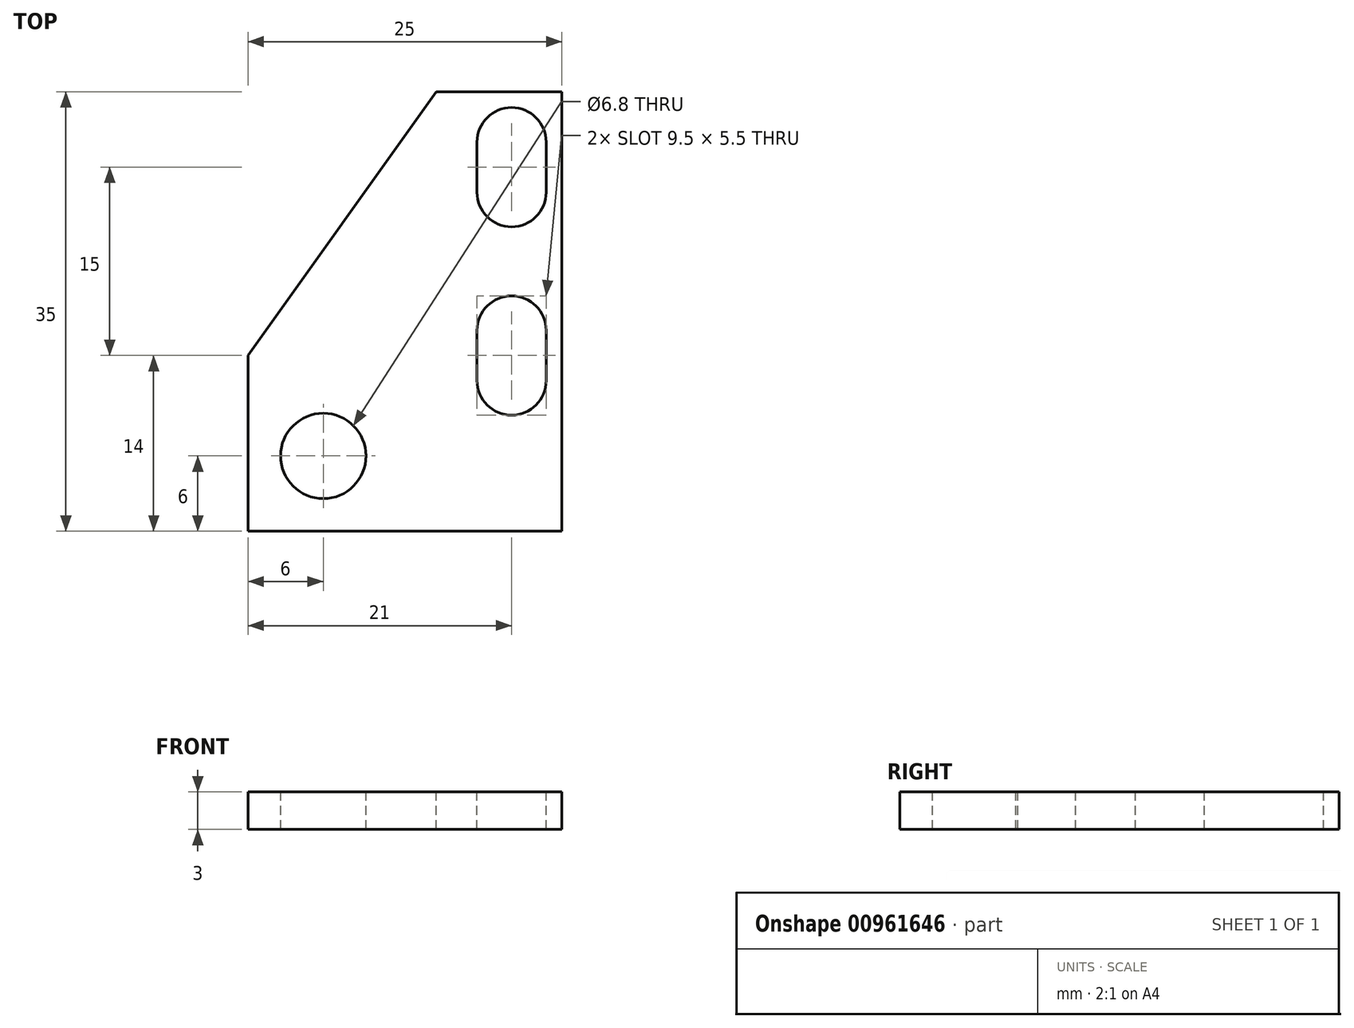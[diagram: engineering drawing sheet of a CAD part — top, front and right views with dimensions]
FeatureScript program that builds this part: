
annotation { "Feature Type Name" : "Feature", "Feature Type Description" : "" }
export const myFeature = defineFeature(function(context is Context, id is Id, definition is map)
    precondition{}
    {
        {
            var Q0;
            Q0=qCreatedBy(makeId("Top.planeOp"),FACE);
            var sketch = newSketch(context, id + "F0", { "sketchPlane" : qUnion([Q0])});
            skLineSegment(sketch, "E0.bottom", {"start": v(0, 0) * mm, "end": v(25, 0) * mm});
            skLineSegment(sketch, "E0.top", {"start": v(0, -35) * mm, "end": v(25, -35) * mm});
            skLineSegment(sketch, "E0.left", {"start": v(0, 0) * mm, "end": v(0, -35) * mm});
            skLineSegment(sketch, "E0.right", {"start": v(25, 0) * mm, "end": v(25, -35) * mm});
            skSolve(sketch);
        }
        {
            var Q0;
            Q0=makeQuery(id+"F0.imprint","IMPRINT",FACE,{"disambiguationData":[TD([[makeQuery(id+"F0.imprint","IMPRINT",EDGE,{"derivedFrom":sQuery(id+"F0.wireOp",EDGE,"E0.bottom")}),-1.0]])]});
            extrude(context, id + "F1", {"entities" : qUnion([Q0]), "depth" : 3 * mm, "offsetDistance" : 25 * mm});
        }
        {
            var Q0;
            Q0=makeQuery(id+"F1.opExtrude","CAP_FACE",FACE,{"disambiguationData":[OSD([sQuery(id+"F0.wireOp",EDGE,"E0.bottom"),sQuery(id+"F0.wireOp",EDGE,"E0.top"),sQuery(id+"F0.wireOp",EDGE,"E0.left"),sQuery(id+"F0.wireOp",EDGE,"E0.right")])],"isStart":false});
            var sketch = newSketch(context, id + "F2", { "sketchPlane" : qUnion([Q0])});
            skPoint(sketch, "E1", {"position": v(21, -4) * mm});
            skPoint(sketch, "E2", {"position": v(21, -19) * mm});
            skPoint(sketch, "E3", {"position": v(0, -35) * mm});
            skPoint(sketch, "E4", {"position": v(6, -29) * mm});
            skPoint(sketch, "E5", {"position": v(21, -8) * mm});
            skPoint(sketch, "E6", {"position": v(21, -23) * mm});
            skPoint(sketch, "E7", {"position": v(17.74, 0) * mm});
            skCircle(sketch, "E8", {"center": v(21, -4) * mm, "radius": 2.75 * mm});
            skCircle(sketch, "E9", {"center": v(21, -8) * mm, "radius": 2.75 * mm});
            skCircle(sketch, "E10", {"center": v(21, -19) * mm, "radius": 2.75 * mm});
            skCircle(sketch, "E11", {"center": v(21, -23) * mm, "radius": 2.75 * mm});
            skLineSegment(sketch, "E12", {"start": v(18.25, -8) * mm, "end": v(18.25, -4) * mm});
            skLineSegment(sketch, "E13", {"start": v(18.25, -4) * mm, "end": v(23.75, -4) * mm});
            skLineSegment(sketch, "E14", {"start": v(23.75, -4) * mm, "end": v(23.75, -8) * mm});
            skLineSegment(sketch, "E15", {"start": v(18.25, -19) * mm, "end": v(18.25, -23) * mm});
            skLineSegment(sketch, "E16", {"start": v(23.75, -19) * mm, "end": v(23.75, -23) * mm});
            skSolve(sketch);
        }
        {
            var Q0;
            Q0 = qSketchRegion(id + "F2", true);
            var Q1;
            {var subQ0=sQuery(id+"F2.wireOp",EDGE,"E11");var subQ1=sQuery(id+"F2.wireOp",EDGE,"E10");var subQ2=makeQuery(id+"F2.imprint","INTERSECT",VERTEX,{"disambiguationData":[OD(0.0)],"derivedFrom":[subQ1,subQ0]});Q1=makeQuery(id+"F2.imprint","IMPRINT",FACE,{"disambiguationData":[TD([[makeQuery(id+"F2.imprint","IMPRINT",EDGE,{"disambiguationData":[TD([[subQ2,-1.0]])],"derivedFrom":subQ1}),1.0]])]});}
            var Q2;
            {var subQ0=sQuery(id+"F2.wireOp",EDGE,"E9");var subQ1=sQuery(id+"F2.wireOp",EDGE,"E8");var subQ2=makeQuery(id+"F2.imprint","INTERSECT",VERTEX,{"disambiguationData":[OD(0.0)],"derivedFrom":[subQ1,subQ0]});Q2=makeQuery(id+"F2.imprint","IMPRINT",FACE,{"disambiguationData":[TD([[makeQuery(id+"F2.imprint","IMPRINT",EDGE,{"disambiguationData":[TD([[subQ2,-1.0]])],"derivedFrom":subQ1}),1.0]])]});}
            extrude(context, id + "F3", {"entities" : qUnion([Q0, Q1, Q2]), "operationType" : NewBodyOperationType.REMOVE, "oppositeDirection" : true, "depth" : 25 * mm, "offsetDistance" : 25 * mm});
        }
        {
            var Q0;
            Q0=sQuery(id+"F2.wireOp",VERTEX,"E4");
            var Q1;
            Q1=makeQuery(id+"F1.opExtrude","SWEPT_BODY",BODY,{"disambiguationData":[OSD([sQuery(id+"F0.wireOp",EDGE,"E0.bottom"),sQuery(id+"F0.wireOp",EDGE,"E0.top"),sQuery(id+"F0.wireOp",EDGE,"E0.left"),sQuery(id+"F0.wireOp",EDGE,"E0.right")])]});
            hole(context, id + "F4", {"style" : HoleStyle.SIMPLE, "endStyle" : HoleEndStyle.BLIND, "standardTappedOrClearance" : lookupTablePath({ "standard" : "ISO", "engagement" : "75%", "pitch" : "1.25 mm", "size" : "M8", "type" : "Tapped" }), "standardBlindInLast" : lookupTablePath({ "standard" : "ISO", "fit" : "Normal", "engagement" : "75%", "pitch" : "1.25 mm", "size" : "M8", "type" : "Clearance & tapped" }), "holeDiameter" : 6.8 * mm, "majorDiameter" : 8 * mm, "showTappedDepth" : true, "holeDepth" : 16.35 * mm, "isTappedThrough" : true, "tappedDepth" : 12.6 * mm, "tapClearance" : 3, "startFromSketch" : true, "locations" : qUnion([Q0]), "scope" : qUnion([Q1])});
        }
        {
            var Q0;
            {var subQ1=sQuery(id+"F2.wireOp",EDGE,"E12");Q0=makeQuery(id+"F2.imprint","IMPRINT",FACE,{"disambiguationData":[TD([[makeQuery(id+"F2.imprint","IMPRINT",EDGE,{"derivedFrom":subQ1}),1.0]])]});}
            var sketch = newSketch(context, id + "F5", { "sketchPlane" : qUnion([Q0])});
            skPoint(sketch, "E17", {"position": v(15, 0) * mm});
            skPoint(sketch, "E18", {"position": v(0, -21) * mm});
            skLineSegment(sketch, "E19", {"start": v(15, 0) * mm, "end": v(0, -21) * mm});
            skLineSegment(sketch, "E20", {"start": v(0, -21) * mm, "end": v(0, 0) * mm});
            skLineSegment(sketch, "E21", {"start": v(0, 0) * mm, "end": v(15, 0) * mm});
            skSolve(sketch);
        }
        {
            var Q0;
            Q0 = qSketchRegion(id + "F5", true);
            extrude(context, id + "F6", {"entities" : qUnion([Q0]), "operationType" : NewBodyOperationType.REMOVE, "oppositeDirection" : true, "depth" : 25 * mm, "offsetDistance" : 25 * mm});
        }
    });
